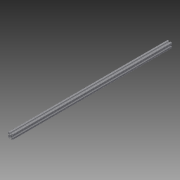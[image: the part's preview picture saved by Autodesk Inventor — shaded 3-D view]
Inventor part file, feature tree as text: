
AUTODESK INVENTOR PART (.ipt)
format: ipt  version: 2013 (Build 170138000, 138)  size: 288,768 bytes
history: native  units: in
note: dims shown in document units (in); Inventor stores cm internally (conversion verified against a paired STEP export)
features: extrude x1, sketch x1
ambient origin geometry x8: Origin, YZ Plane, XZ Plane, XY Plane, X Axis, Y Axis, Z Axis, Center Point
bodies: Solid1 (feature_tree)
feature tree (2):
  extrude  "Extrusion1"  [1 undecoded]
  sketch  "Sketch1"  dims[d0=49.0in d1=0.0in]
note: 1 required parameter value undecoded (feature->parameter linkage not recoverable at this tier; creation-order binding heuristic only, values carry confidence <= 0.55)
